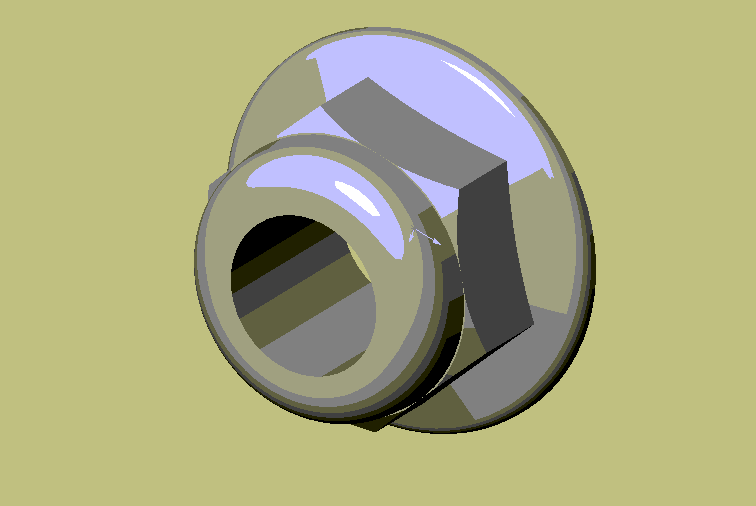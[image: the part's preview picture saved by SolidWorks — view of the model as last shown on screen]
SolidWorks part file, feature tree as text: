
SOLIDWORKS PART (.sldprt)
format: sldprt  version: not decoded by parser v0  size: 236,032 bytes
history: native  units: mm
features: sketch x6, plane x4, extrude x4, cut_extrude x2, fillet x2, material x1, chamfer x1 (+8 scaffold rows collapsed)
feature tree (28):
  scaffold x8  (default folders/planes/origin — collapsed)
  material  "Matériau <non spécifié>"
  plane  "Plane1"
  plane  "Plane2"
  plane  "Plane3"
  sketch  "Esquisse1"  dims[D2=4.0mm D1=7.0mm]
  sketch  "Esquisse3"
  extrude  "Base-Extrusion"  Depth=3.5mm
  chamfer  "Chanfrein1"  Distance=0.5mm Angle=45deg
  cut_extrude  "Enlèv. mat.-Extru.4"  [1 undecoded]
  plane  "Plan1"  Offset=0.5mm
  sketch  "Esquisse5"  dims[D1=10.0mm]
  extrude  "Boss.-Extru.1"  Depth=1mm
  sketch  "Esquisse6"
  extrude  "Boss.-Extru.2"  Depth=0.5mm
  sketch  "Esquisse7"  dims[D1=7.0mm]
  extrude  "Boss.-Extru.3"  Depth=1.5mm
  fillet  "Congé1"  Radius=1mm
  fillet  "Congé2"  Radius=0.5mm
  sketch  "Esquisse8"  dims[D1=4.0mm]
  cut_extrude  "Enlèv. mat.-Extru.5"  [1 undecoded]
decode coverage: 11 of 15 modeling features carry decoded parameters
note: 2 parameter values undecoded
note: suppression state not decoded; provenance and decode notes live in map.json
